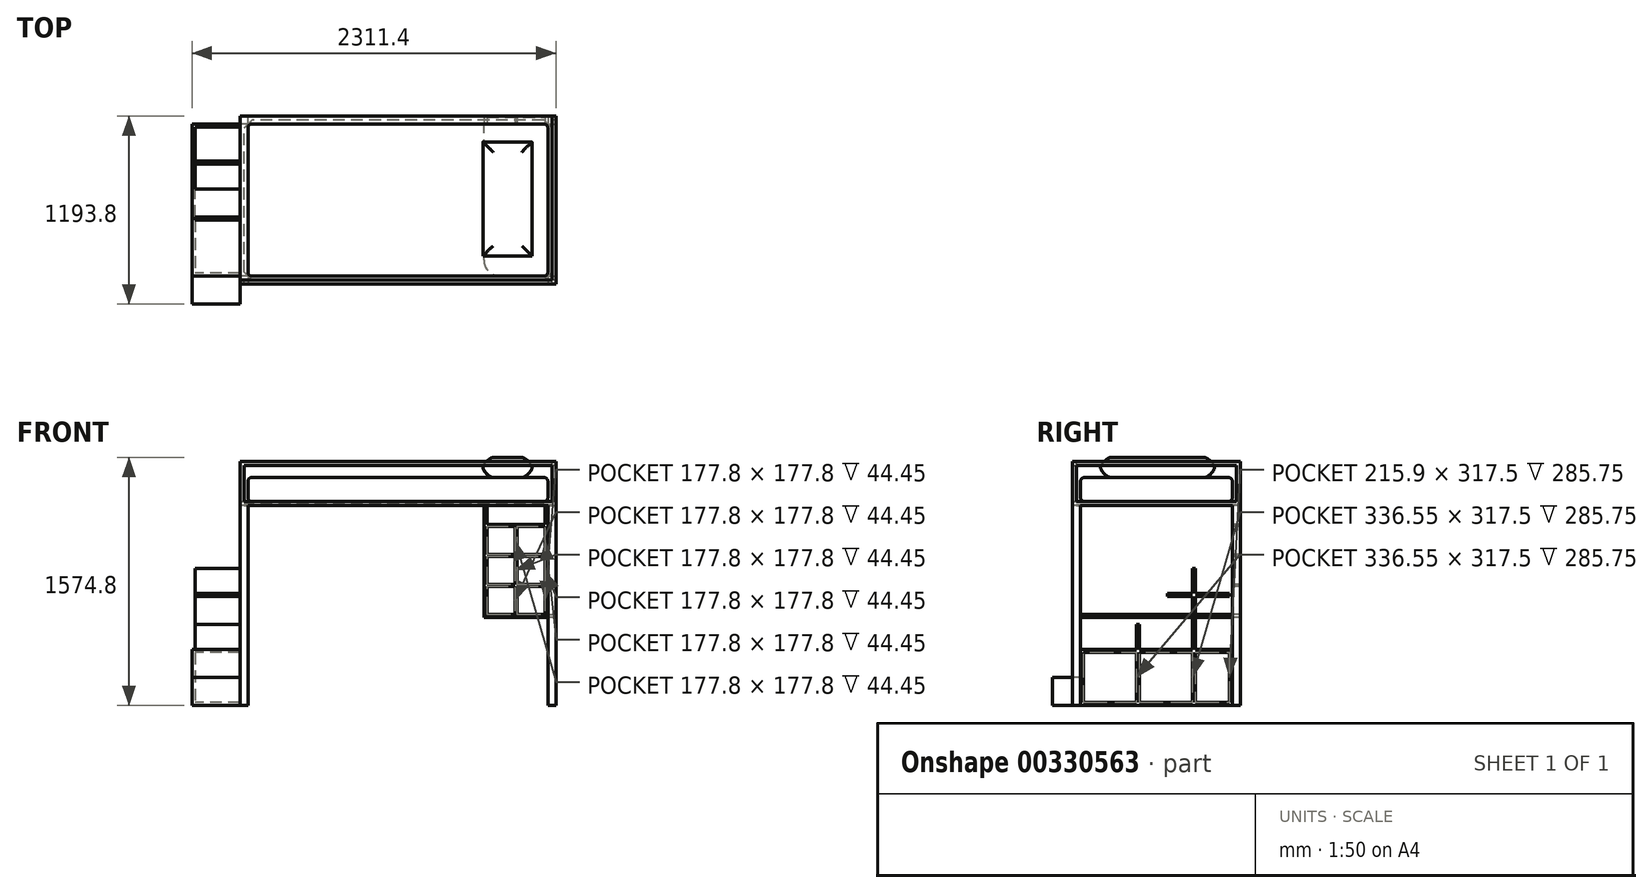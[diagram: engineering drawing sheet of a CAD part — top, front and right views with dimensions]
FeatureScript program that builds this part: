
annotation { "Feature Type Name" : "Feature", "Feature Type Description" : "" }
export const myFeature = defineFeature(function(context is Context, id is Id, definition is map)
    precondition{}
    {
        {
            var Q0;
            Q0=qCreatedBy(makeId("Top.planeOp"),FACE);
            var sketch = newSketch(context, id + "F0", { "sketchPlane" : qUnion([Q0])});
            skLineSegment(sketch, "E0.bottom", {"start": v(-952.5, 482.6) * mm, "end": v(952.5, 482.6) * mm});
            skLineSegment(sketch, "E0.top", {"start": v(-952.5, -482.6) * mm, "end": v(952.5, -482.6) * mm});
            skLineSegment(sketch, "E0.left", {"start": v(-952.5, 482.6) * mm, "end": v(-952.5, -482.6) * mm});
            skLineSegment(sketch, "E0.right", {"start": v(952.5, 482.6) * mm, "end": v(952.5, -482.6) * mm});
            skPoint(sketch, "E0.middle", {"position": v(0, 0) * mm});
            skLineSegment(sketch, "E1.bottom", {"start": v(-952.5, 482.6) * mm, "end": v(-1003.3, 482.6) * mm});
            skLineSegment(sketch, "E1.top", {"start": v(-952.5, 533.4) * mm, "end": v(-1003.3, 533.4) * mm});
            skLineSegment(sketch, "E1.left", {"start": v(-952.5, 482.6) * mm, "end": v(-952.5, 533.4) * mm});
            skLineSegment(sketch, "E1.right", {"start": v(-1003.3, 482.6) * mm, "end": v(-1003.3, 533.4) * mm});
            skLineSegment(sketch, "E2.bottom", {"start": v(-952.5, -482.6) * mm, "end": v(-1003.3, -482.6) * mm});
            skLineSegment(sketch, "E2.top", {"start": v(-952.5, -533.4) * mm, "end": v(-1003.3, -533.4) * mm});
            skLineSegment(sketch, "E2.left", {"start": v(-952.5, -482.6) * mm, "end": v(-952.5, -533.4) * mm});
            skLineSegment(sketch, "E2.right", {"start": v(-1003.3, -482.6) * mm, "end": v(-1003.3, -533.4) * mm});
            skLineSegment(sketch, "E3.bottom", {"start": v(952.5, 482.6) * mm, "end": v(1003.3, 482.6) * mm});
            skLineSegment(sketch, "E3.top", {"start": v(952.5, 533.4) * mm, "end": v(1003.3, 533.4) * mm});
            skLineSegment(sketch, "E3.left", {"start": v(952.5, 482.6) * mm, "end": v(952.5, 533.4) * mm});
            skLineSegment(sketch, "E3.right", {"start": v(1003.3, 482.6) * mm, "end": v(1003.3, 533.4) * mm});
            skLineSegment(sketch, "E4.bottom", {"start": v(952.5, -482.6) * mm, "end": v(1003.3, -482.6) * mm});
            skLineSegment(sketch, "E4.top", {"start": v(952.5, -533.4) * mm, "end": v(1003.3, -533.4) * mm});
            skLineSegment(sketch, "E4.left", {"start": v(952.5, -482.6) * mm, "end": v(952.5, -533.4) * mm});
            skLineSegment(sketch, "E4.right", {"start": v(1003.3, -482.6) * mm, "end": v(1003.3, -533.4) * mm});
            skSolve(sketch);
        }
        {
            var Q0;
            Q0=makeQuery(id+"F0.imprint","IMPRINT",FACE,{"disambiguationData":[TD([[makeQuery(id+"F0.imprint","IMPRINT",EDGE,{"derivedFrom":sQuery(id+"F0.wireOp",EDGE,"E1.bottom")}),-1.0]])]});
            var Q1;
            Q1=makeQuery(id+"F0.imprint","IMPRINT",FACE,{"disambiguationData":[TD([[makeQuery(id+"F0.imprint","IMPRINT",EDGE,{"derivedFrom":sQuery(id+"F0.wireOp",EDGE,"E2.bottom")}),1.0]])]});
            var Q2;
            Q2=makeQuery(id+"F0.imprint","IMPRINT",FACE,{"disambiguationData":[TD([[makeQuery(id+"F0.imprint","IMPRINT",EDGE,{"derivedFrom":sQuery(id+"F0.wireOp",EDGE,"E3.bottom")}),1.0]])]});
            var Q3;
            Q3=makeQuery(id+"F0.imprint","IMPRINT",FACE,{"disambiguationData":[TD([[makeQuery(id+"F0.imprint","IMPRINT",EDGE,{"derivedFrom":sQuery(id+"F0.wireOp",EDGE,"E4.bottom")}),-1.0]])]});
            extrude(context, id + "F1", {"entities" : qUnion([Q0, Q1, Q2, Q3]), "depth" : 1270 * mm});
        }
        {
            var Q0;
            Q0=makeQuery(id+"F1.opExtrude","SWEPT_FACE",FACE,{"disambiguationData":[OSD([sQuery(id+"F0.wireOp",EDGE,"E1.right")])]});
            cPlane(context, id + "F2", {"entities" : qUnion([Q0]), "cplaneType" : CPlaneType.OFFSET, "offset" : 304.8 * mm, "width" : 152.4 * mm, "height" : 152.4 * mm});
        }
        {
            var Q0;
            Q0=qCreatedBy(id+"F2.planeOp",FACE);
            var sketch = newSketch(context, id + "F3", { "sketchPlane" : qUnion([Q0])});
            skPoint(sketch, "E5.0", {"position": v(-482.6, 0) * mm});
            skPoint(sketch, "E6.0", {"position": v(482.6, 0) * mm});
            skLineSegment(sketch, "E7.bottom", {"start": v(-482.6, 0) * mm, "end": v(482.6, 0) * mm});
            skLineSegment(sketch, "E7.top", {"start": v(-482.6, 355.6) * mm, "end": v(482.6, 355.6) * mm});
            skLineSegment(sketch, "E7.left", {"start": v(-482.6, 0) * mm, "end": v(-482.6, 355.6) * mm});
            skLineSegment(sketch, "E7.right", {"start": v(482.6, 0) * mm, "end": v(482.6, 147.48) * mm});
            skLineSegment(sketch, "E8.bottom", {"start": v(-482.6, 355.6) * mm, "end": v(127, 355.6) * mm});
            skLineSegment(sketch, "E8.top", {"start": v(-482.6, 711.2) * mm, "end": v(127, 711.2) * mm});
            skLineSegment(sketch, "E8.left", {"start": v(-482.6, 355.6) * mm, "end": v(-482.6, 711.2) * mm});
            skLineSegment(sketch, "E8.right", {"start": v(127, 355.6) * mm, "end": v(127, 711.2) * mm});
            skLineSegment(sketch, "E9.bottom", {"start": v(-482.6, 711.2) * mm, "end": v(-228.6, 711.2) * mm});
            skLineSegment(sketch, "E9.top", {"start": v(-482.6, 1066.8) * mm, "end": v(-228.6, 1066.8) * mm});
            skLineSegment(sketch, "E9.left", {"start": v(-482.6, 711.2) * mm, "end": v(-482.6, 1066.8) * mm});
            skLineSegment(sketch, "E9.right", {"start": v(-228.6, 711.2) * mm, "end": v(-228.6, 1066.8) * mm});
            skLineSegment(sketch, "E10.bottom", {"start": v(127, 355.6) * mm, "end": v(304.8, 355.6) * mm});
            skLineSegment(sketch, "E10.top", {"start": v(127, 533.4) * mm, "end": v(304.8, 533.4) * mm});
            skLineSegment(sketch, "E10.left", {"start": v(127, 355.6) * mm, "end": v(127, 533.4) * mm});
            skLineSegment(sketch, "E10.right", {"start": v(304.8, 355.6) * mm, "end": v(304.8, 533.4) * mm});
            skLineSegment(sketch, "E11.bottom", {"start": v(482.6, 0) * mm, "end": v(660.4, 0) * mm});
            skLineSegment(sketch, "E11.top", {"start": v(482.6, 177.8) * mm, "end": v(660.4, 177.8) * mm});
            skLineSegment(sketch, "E11.left", {"start": v(482.6, 0) * mm, "end": v(482.6, 177.8) * mm});
            skLineSegment(sketch, "E11.right", {"start": v(660.4, 0) * mm, "end": v(660.4, 177.8) * mm});
            skLineSegment(sketch, "E12.bottom", {"start": v(-228.6, 711.2) * mm, "end": v(-50.8, 711.2) * mm});
            skLineSegment(sketch, "E12.top", {"start": v(-228.6, 889) * mm, "end": v(-50.8, 889) * mm});
            skLineSegment(sketch, "E12.left", {"start": v(-228.6, 711.2) * mm, "end": v(-228.6, 889) * mm});
            skLineSegment(sketch, "E12.right", {"start": v(-50.8, 711.2) * mm, "end": v(-50.8, 889) * mm});
            skLineSegment(sketch, "E13", {"start": v(482.6, 355.6) * mm, "end": v(482.6, 177.8) * mm});
            skSolve(sketch);
        }
        {
            var Q0;
            Q0=makeQuery(id+"F3.imprint","IMPRINT",FACE,{"disambiguationData":[TD([[makeQuery(id+"F3.imprint","IMPRINT",EDGE,{"derivedFrom":sQuery(id+"F3.wireOp",EDGE,"E9.bottom")}),1.0]])]});
            var Q1;
            Q1=makeQuery(id+"F3.imprint","IMPRINT",FACE,{"disambiguationData":[TD([[makeQuery(id+"F3.imprint","IMPRINT",EDGE,{"derivedFrom":sQuery(id+"F3.wireOp",EDGE,"E12.bottom")}),1.0]])]});
            var Q2;
            Q2=makeQuery(id+"F3.imprint","IMPRINT",FACE,{"disambiguationData":[TD([[makeQuery(id+"F3.imprint","IMPRINT",EDGE,{"derivedFrom":sQuery(id+"F3.wireOp",EDGE,"E8.bottom")}),1.0]])]});
            var Q3;
            Q3=makeQuery(id+"F3.imprint","IMPRINT",FACE,{"disambiguationData":[TD([[makeQuery(id+"F3.imprint","IMPRINT",EDGE,{"derivedFrom":sQuery(id+"F3.wireOp",EDGE,"E10.bottom")}),1.0]])]});
            var Q4;
            {var subQ1=sQuery(id+"F3.wireOp",EDGE,"E7.bottom");Q4=makeQuery(id+"F3.imprint","IMPRINT",FACE,{"disambiguationData":[TD([[makeQuery(id+"F3.imprint","IMPRINT",EDGE,{"derivedFrom":subQ1}),1.0]])]});}
            var Q5;
            {var subQ3=sQuery(id+"F3.wireOp",EDGE,"E11.bottom");Q5=makeQuery(id+"F3.imprint","IMPRINT",FACE,{"disambiguationData":[TD([[makeQuery(id+"F3.imprint","IMPRINT",EDGE,{"derivedFrom":subQ3}),1.0]])]});}
            extrude(context, id + "F4", {"entities" : qUnion([Q0, Q1, Q2, Q3, Q4, Q5]), "oppositeDirection" : true, "depth" : 19.05 * mm});
        }
        {
            var Q0;
            Q0=makeQuery(id+"F4.opExtrude","CAP_FACE",FACE,{"disambiguationData":[OSD([sQuery(id+"F3.wireOp",EDGE,"E7.bottom"),sQuery(id+"F3.wireOp",EDGE,"E7.top"),sQuery(id+"F3.wireOp",EDGE,"E7.left"),sQuery(id+"F3.wireOp",EDGE,"E8.top"),sQuery(id+"F3.wireOp",EDGE,"E8.left"),sQuery(id+"F3.wireOp",EDGE,"E8.right"),sQuery(id+"F3.wireOp",EDGE,"E9.top"),sQuery(id+"F3.wireOp",EDGE,"E9.left"),sQuery(id+"F3.wireOp",EDGE,"E9.right"),sQuery(id+"F3.wireOp",EDGE,"E10.top"),sQuery(id+"F3.wireOp",EDGE,"E10.right"),sQuery(id+"F3.wireOp",EDGE,"E11.bottom"),sQuery(id+"F3.wireOp",EDGE,"E11.top"),sQuery(id+"F3.wireOp",EDGE,"E11.right"),sQuery(id+"F3.wireOp",EDGE,"E12.top"),sQuery(id+"F3.wireOp",EDGE,"E12.right"),sQuery(id+"F3.wireOp",EDGE,"E13")])],"isStart":false});
            var sketch = newSketch(context, id + "F5", { "sketchPlane" : qUnion([Q0])});
            skLineSegment(sketch, "E14.0", {"start": v(-463.55, 19.05) * mm, "end": v(463.55, 19.05) * mm});
            skLineSegment(sketch, "E14.1", {"start": v(69.85, 869.95) * mm, "end": v(69.85, 692.15) * mm});
            skLineSegment(sketch, "E14.2", {"start": v(247.65, 869.95) * mm, "end": v(69.85, 869.95) * mm});
            skLineSegment(sketch, "E14.3", {"start": v(247.65, 1047.75) * mm, "end": v(247.65, 869.95) * mm});
            skLineSegment(sketch, "E14.4", {"start": v(463.55, 1047.75) * mm, "end": v(247.65, 1047.75) * mm});
            skLineSegment(sketch, "E14.5", {"start": v(69.85, 692.15) * mm, "end": v(-107.95, 692.15) * mm});
            skLineSegment(sketch, "E14.6", {"start": v(463.55, 19.05) * mm, "end": v(463.55, 1047.75) * mm});
            skLineSegment(sketch, "E14.7", {"start": v(-107.95, 692.15) * mm, "end": v(-107.95, 514.35) * mm});
            skLineSegment(sketch, "E14.8", {"start": v(-107.95, 514.35) * mm, "end": v(-285.75, 514.35) * mm});
            skLineSegment(sketch, "E14.9", {"start": v(-285.75, 514.35) * mm, "end": v(-285.75, 336.55) * mm});
            skLineSegment(sketch, "E14.10", {"start": v(-285.75, 336.55) * mm, "end": v(-463.55, 336.55) * mm});
            skLineSegment(sketch, "E14.11", {"start": v(-463.55, 336.55) * mm, "end": v(-463.55, 19.05) * mm});
            skLineSegment(sketch, "E15.0.0", {"start": v(482.6, 0) * mm, "end": v(482.6, 1066.8) * mm});
            skLineSegment(sketch, "E15.0.1", {"start": v(482.6, 1066.8) * mm, "end": v(228.6, 1066.8) * mm});
            skLineSegment(sketch, "E15.0.2", {"start": v(228.6, 1066.8) * mm, "end": v(228.6, 889) * mm});
            skLineSegment(sketch, "E15.0.3", {"start": v(228.6, 889) * mm, "end": v(50.8, 889) * mm});
            skLineSegment(sketch, "E15.0.4", {"start": v(50.8, 889) * mm, "end": v(50.8, 711.2) * mm});
            skLineSegment(sketch, "E15.0.5", {"start": v(50.8, 711.2) * mm, "end": v(-127, 711.2) * mm});
            skLineSegment(sketch, "E15.0.6", {"start": v(-127, 711.2) * mm, "end": v(-127, 533.4) * mm});
            skLineSegment(sketch, "E15.0.7", {"start": v(-127, 533.4) * mm, "end": v(-304.8, 533.4) * mm});
            skLineSegment(sketch, "E15.0.8", {"start": v(-304.8, 533.4) * mm, "end": v(-304.8, 355.6) * mm});
            skLineSegment(sketch, "E15.0.9", {"start": v(-304.8, 355.6) * mm, "end": v(-482.6, 355.6) * mm});
            skLineSegment(sketch, "E15.0.10", {"start": v(-482.6, 355.6) * mm, "end": v(-482.6, 177.8) * mm});
            skLineSegment(sketch, "E15.0.11", {"start": v(-482.6, 177.8) * mm, "end": v(-660.4, 177.8) * mm});
            skLineSegment(sketch, "E15.0.12", {"start": v(-660.4, 177.8) * mm, "end": v(-660.4, 0) * mm});
            skLineSegment(sketch, "E15.0.13", {"start": v(-660.4, 0) * mm, "end": v(482.6, 0) * mm});
            skSolve(sketch);
        }
        {
            var Q0;
            Q0=makeQuery(id+"F5.imprint","IMPRINT",FACE,{"disambiguationData":[TD([[makeQuery(id+"F5.imprint","IMPRINT",EDGE,{"derivedFrom":sQuery(id+"F5.wireOp",EDGE,"E14.0")}),-1.0]])]});
            extrude(context, id + "F6", {"entities" : qUnion([Q0]), "operationType" : NewBodyOperationType.ADD, "depth" : 285.75 * mm});
        }
        {
            var Q0;
            Q0=makeQuery(id+"F4.opExtrude","CAP_FACE",FACE,{"disambiguationData":[OSD([sQuery(id+"F3.wireOp",EDGE,"E7.bottom"),sQuery(id+"F3.wireOp",EDGE,"E7.top"),sQuery(id+"F3.wireOp",EDGE,"E7.left"),sQuery(id+"F3.wireOp",EDGE,"E8.top"),sQuery(id+"F3.wireOp",EDGE,"E8.left"),sQuery(id+"F3.wireOp",EDGE,"E8.right"),sQuery(id+"F3.wireOp",EDGE,"E9.top"),sQuery(id+"F3.wireOp",EDGE,"E9.left"),sQuery(id+"F3.wireOp",EDGE,"E9.right"),sQuery(id+"F3.wireOp",EDGE,"E10.top"),sQuery(id+"F3.wireOp",EDGE,"E10.right"),sQuery(id+"F3.wireOp",EDGE,"E11.bottom"),sQuery(id+"F3.wireOp",EDGE,"E11.top"),sQuery(id+"F3.wireOp",EDGE,"E11.right"),sQuery(id+"F3.wireOp",EDGE,"E12.top"),sQuery(id+"F3.wireOp",EDGE,"E12.right"),sQuery(id+"F3.wireOp",EDGE,"E13")])],"isStart":false});
            var sketch = newSketch(context, id + "F7", { "sketchPlane" : qUnion([Q0])});
            skLineSegment(sketch, "E16.bottom", {"start": v(-285.75, 336.55) * mm, "end": v(463.55, 336.55) * mm});
            skLineSegment(sketch, "E16.top", {"start": v(-285.75, 355.6) * mm, "end": v(463.55, 355.6) * mm});
            skLineSegment(sketch, "E16.left", {"start": v(-285.75, 336.55) * mm, "end": v(-285.75, 355.6) * mm});
            skLineSegment(sketch, "E16.right", {"start": v(463.55, 336.55) * mm, "end": v(463.55, 355.6) * mm});
            skLineSegment(sketch, "E17.bottom", {"start": v(-107.95, 514.35) * mm, "end": v(-127, 514.35) * mm});
            skLineSegment(sketch, "E17.top", {"start": v(-107.95, 19.05) * mm, "end": v(-127, 19.05) * mm});
            skLineSegment(sketch, "E17.left", {"start": v(-107.95, 514.35) * mm, "end": v(-107.95, 19.05) * mm});
            skLineSegment(sketch, "E17.right", {"start": v(-127, 514.35) * mm, "end": v(-127, 19.05) * mm});
            skLineSegment(sketch, "E18.bottom", {"start": v(247.65, 869.95) * mm, "end": v(228.6, 869.95) * mm});
            skLineSegment(sketch, "E18.top", {"start": v(247.65, 19.05) * mm, "end": v(228.6, 19.05) * mm});
            skLineSegment(sketch, "E18.left", {"start": v(247.65, 869.95) * mm, "end": v(247.65, 19.05) * mm});
            skLineSegment(sketch, "E18.right", {"start": v(228.6, 869.95) * mm, "end": v(228.6, 19.05) * mm});
            skLineSegment(sketch, "E19.bottom", {"start": v(69.85, 692.15) * mm, "end": v(463.55, 692.15) * mm});
            skLineSegment(sketch, "E19.top", {"start": v(69.85, 711.2) * mm, "end": v(463.55, 711.2) * mm});
            skLineSegment(sketch, "E19.left", {"start": v(69.85, 692.15) * mm, "end": v(69.85, 711.2) * mm});
            skLineSegment(sketch, "E19.right", {"start": v(463.55, 692.15) * mm, "end": v(463.55, 711.2) * mm});
            skSolve(sketch);
        }
        {
            var Q0;
            Q0 = qSketchRegion(id + "F7", true);
            extrude(context, id + "F8", {"entities" : qUnion([Q0]), "operationType" : NewBodyOperationType.ADD, "depth" : 285.75 * mm});
        }
        {
            var Q0;
            Q0=makeQuery(id+"F1.opExtrude","CAP_FACE",FACE,{"disambiguationData":[OSD([sQuery(id+"F0.wireOp",EDGE,"E1.bottom"),sQuery(id+"F0.wireOp",EDGE,"E1.top"),sQuery(id+"F0.wireOp",EDGE,"E1.left"),sQuery(id+"F0.wireOp",EDGE,"E1.right")])],"isStart":false});
            var sketch = newSketch(context, id + "F9", { "sketchPlane" : qUnion([Q0])});
            skPoint(sketch, "E20.0", {"position": v(1003.3, -533.4) * mm});
            skPoint(sketch, "E21.0", {"position": v(-1003.3, 533.4) * mm});
            skLineSegment(sketch, "E22.bottom", {"start": v(-1003.3, 533.4) * mm, "end": v(1003.3, 533.4) * mm});
            skLineSegment(sketch, "E22.top", {"start": v(-1003.3, -533.4) * mm, "end": v(1003.3, -533.4) * mm});
            skLineSegment(sketch, "E22.left", {"start": v(-1003.3, 533.4) * mm, "end": v(-1003.3, -533.4) * mm});
            skLineSegment(sketch, "E22.right", {"start": v(1003.3, 533.4) * mm, "end": v(1003.3, -533.4) * mm});
            skLineSegment(sketch, "E23.0.0", {"start": v(1003.3, -482.6) * mm, "end": v(952.5, -482.6) * mm});
            skLineSegment(sketch, "E23.0.1", {"start": v(952.5, -482.6) * mm, "end": v(952.5, -533.4) * mm});
            skLineSegment(sketch, "E23.0.2", {"start": v(952.5, -533.4) * mm, "end": v(1003.3, -533.4) * mm});
            skLineSegment(sketch, "E23.0.3", {"start": v(1003.3, -533.4) * mm, "end": v(1003.3, -482.6) * mm});
            skLineSegment(sketch, "E24.0.0", {"start": v(1003.3, 533.4) * mm, "end": v(952.5, 533.4) * mm});
            skLineSegment(sketch, "E24.0.1", {"start": v(952.5, 533.4) * mm, "end": v(952.5, 482.6) * mm});
            skLineSegment(sketch, "E24.0.2", {"start": v(952.5, 482.6) * mm, "end": v(1003.3, 482.6) * mm});
            skLineSegment(sketch, "E24.0.3", {"start": v(1003.3, 482.6) * mm, "end": v(1003.3, 533.4) * mm});
            skLineSegment(sketch, "E25.0.0", {"start": v(-952.5, -533.4) * mm, "end": v(-952.5, -482.6) * mm});
            skLineSegment(sketch, "E25.0.1", {"start": v(-952.5, -482.6) * mm, "end": v(-1003.3, -482.6) * mm});
            skLineSegment(sketch, "E25.0.2", {"start": v(-1003.3, -482.6) * mm, "end": v(-1003.3, -533.4) * mm});
            skLineSegment(sketch, "E25.0.3", {"start": v(-1003.3, -533.4) * mm, "end": v(-952.5, -533.4) * mm});
            skLineSegment(sketch, "E26.0.0", {"start": v(-952.5, 482.6) * mm, "end": v(-952.5, 533.4) * mm});
            skLineSegment(sketch, "E26.0.1", {"start": v(-952.5, 533.4) * mm, "end": v(-1003.3, 533.4) * mm});
            skLineSegment(sketch, "E26.0.2", {"start": v(-1003.3, 533.4) * mm, "end": v(-1003.3, 482.6) * mm});
            skLineSegment(sketch, "E26.0.3", {"start": v(-1003.3, 482.6) * mm, "end": v(-952.5, 482.6) * mm});
            skPoint(sketch, "E27.firstSnap0", {"position": v(952.5, -508) * mm});
            skPoint(sketch, "E27.firstSnap1", {"position": v(977.9, -482.6) * mm});
            skPoint(sketch, "E27.oppositeSnap0", {"position": v(-1003.3, 508) * mm});
            skPoint(sketch, "E27.oppositeSnap1", {"position": v(-977.9, 533.4) * mm});
            skLineSegment(sketch, "E27.bottom", {"start": v(977.9, -508) * mm, "end": v(-977.9, -508) * mm});
            skLineSegment(sketch, "E27.top", {"start": v(977.9, 508) * mm, "end": v(-977.9, 508) * mm});
            skLineSegment(sketch, "E27.left", {"start": v(977.9, -508) * mm, "end": v(977.9, 508) * mm});
            skLineSegment(sketch, "E27.right", {"start": v(-977.9, -508) * mm, "end": v(-977.9, 508) * mm});
            skSolve(sketch);
        }
        {
            var Q0;
            Q0 = qSketchRegion(id + "F9", true);
            extrude(context, id + "F10", {"entities" : qUnion([Q0]), "depth" : 25.4 * mm});
        }
        {
            var Q0;
            Q0=makeQuery(id+"F10.opExtrude","CAP_FACE",FACE,{"disambiguationData":[OSD([sQuery(id+"F9.wireOp",EDGE,"E22.bottom"),sQuery(id+"F9.wireOp",EDGE,"E22.top"),sQuery(id+"F9.wireOp",EDGE,"E22.left"),sQuery(id+"F9.wireOp",EDGE,"E22.right")])],"isStart":false});
            var sketch = newSketch(context, id + "F11", { "sketchPlane" : qUnion([Q0])});
            skPoint(sketch, "E28.0", {"position": v(-952.5, 482.6) * mm});
            skPoint(sketch, "E29.0", {"position": v(952.5, -482.6) * mm});
            skLineSegment(sketch, "E30.bottom", {"start": v(-952.5, 482.6) * mm, "end": v(952.5, 482.6) * mm});
            skLineSegment(sketch, "E30.top", {"start": v(-952.5, -482.6) * mm, "end": v(952.5, -482.6) * mm});
            skLineSegment(sketch, "E30.left", {"start": v(-952.5, 482.6) * mm, "end": v(-952.5, -482.6) * mm});
            skLineSegment(sketch, "E30.right", {"start": v(952.5, 482.6) * mm, "end": v(952.5, -482.6) * mm});
            skSolve(sketch);
        }
        {
            var Q0;
            Q0=makeQuery(id+"F11.imprint","IMPRINT",FACE,{"disambiguationData":[TD([[makeQuery(id+"F11.imprint","IMPRINT",EDGE,{"derivedFrom":sQuery(id+"F11.wireOp",EDGE,"E30.bottom")}),-1.0]])]});
            extrude(context, id + "F12", {"entities" : qUnion([Q0]), "depth" : 152.4 * mm});
        }
        {
            var Q0;
            Q0=makeQuery(id+"F12.opExtrude","SWEPT_EDGE",EDGE,{"disambiguationData":[OSD([sQuery(id+"F11.wireOp",EDGE,"E30.top"),sQuery(id+"F11.wireOp",EDGE,"E30.left")])]});
            var Q1;
            Q1=makeQuery(id+"F12.opExtrude","SWEPT_EDGE",EDGE,{"disambiguationData":[OSD([sQuery(id+"F11.wireOp",EDGE,"E30.top"),sQuery(id+"F11.wireOp",EDGE,"E30.right")])]});
            var Q2;
            Q2=makeQuery(id+"F12.opExtrude","SWEPT_EDGE",EDGE,{"disambiguationData":[OSD([sQuery(id+"F11.wireOp",EDGE,"E30.bottom"),sQuery(id+"F11.wireOp",EDGE,"E30.right")])]});
            var Q3;
            Q3=makeQuery(id+"F12.opExtrude","SWEPT_EDGE",EDGE,{"disambiguationData":[OSD([sQuery(id+"F11.wireOp",EDGE,"E30.bottom"),sQuery(id+"F11.wireOp",EDGE,"E30.left")])]});
            var Q4;
            Q4=makeQuery(id+"F12.opExtrude","CAP_EDGE",EDGE,{"disambiguationData":[OSD([sQuery(id+"F11.wireOp",EDGE,"E30.left")])],"isStart":false});
            var Q5;
            Q5=makeQuery(id+"F12.opExtrude","CAP_EDGE",EDGE,{"disambiguationData":[OSD([sQuery(id+"F11.wireOp",EDGE,"E30.bottom")])],"isStart":false});
            var Q6;
            Q6=makeQuery(id+"F12.opExtrude","CAP_EDGE",EDGE,{"disambiguationData":[OSD([sQuery(id+"F11.wireOp",EDGE,"E30.right")])],"isStart":false});
            var Q7;
            Q7=makeQuery(id+"F12.opExtrude","CAP_EDGE",EDGE,{"disambiguationData":[OSD([sQuery(id+"F11.wireOp",EDGE,"E30.top")])],"isStart":false});
            var Q8;
            Q8=makeQuery(id+"F12.opExtrude","CAP_EDGE",EDGE,{"disambiguationData":[OSD([sQuery(id+"F11.wireOp",EDGE,"E30.top")])],"isStart":true});
            var Q9;
            Q9=makeQuery(id+"F12.opExtrude","CAP_EDGE",EDGE,{"disambiguationData":[OSD([sQuery(id+"F11.wireOp",EDGE,"E30.right")])],"isStart":true});
            var Q10;
            Q10=makeQuery(id+"F12.opExtrude","CAP_EDGE",EDGE,{"disambiguationData":[OSD([sQuery(id+"F11.wireOp",EDGE,"E30.bottom")])],"isStart":true});
            var Q11;
            Q11=makeQuery(id+"F12.opExtrude","CAP_EDGE",EDGE,{"disambiguationData":[OSD([sQuery(id+"F11.wireOp",EDGE,"E30.left")])],"isStart":true});
            fillet(context, id + "F13", {"entities" : qUnion([Q0, Q1, Q2, Q3, Q4, Q5, Q6, Q7, Q8, Q9, Q10, Q11]), "radius" : 25.4 * mm, "tangentPropagation" : true, "allowEdgeOverflow" : false});
        }
        {
            var Q0;
            Q0=makeQuery(id+"F10.opExtrude","CAP_FACE",FACE,{"disambiguationData":[OSD([sQuery(id+"F9.wireOp",EDGE,"E22.bottom"),sQuery(id+"F9.wireOp",EDGE,"E22.top"),sQuery(id+"F9.wireOp",EDGE,"E22.left"),sQuery(id+"F9.wireOp",EDGE,"E22.right"),sQuery(id+"F9.wireOp",EDGE,"E23.0.2"),sQuery(id+"F9.wireOp",EDGE,"E23.0.3"),sQuery(id+"F9.wireOp",EDGE,"E24.0.0"),sQuery(id+"F9.wireOp",EDGE,"E24.0.3"),sQuery(id+"F9.wireOp",EDGE,"E25.0.2"),sQuery(id+"F9.wireOp",EDGE,"E25.0.3"),sQuery(id+"F9.wireOp",EDGE,"E26.0.1"),sQuery(id+"F9.wireOp",EDGE,"E26.0.2"),sQuery(id+"F9.wireOp",EDGE,"E27.bottom"),sQuery(id+"F9.wireOp",EDGE,"E27.top"),sQuery(id+"F9.wireOp",EDGE,"E27.left"),sQuery(id+"F9.wireOp",EDGE,"E27.right")])],"isStart":true});
            var sketch = newSketch(context, id + "F14", { "sketchPlane" : qUnion([Q0])});
            skLineSegment(sketch, "E31.0", {"start": v(977.9, 508) * mm, "end": v(-977.9, 508) * mm});
            skLineSegment(sketch, "E32.0", {"start": v(-977.9, 508) * mm, "end": v(-977.9, -508) * mm});
            skLineSegment(sketch, "E33", {"start": v(-977.9, 508) * mm, "end": v(-927.1, 508) * mm});
            skLineSegment(sketch, "E34", {"start": v(-927.1, 508) * mm, "end": v(-977.9, 457.2) * mm});
            skLineSegment(sketch, "E35", {"start": v(-977.9, 457.2) * mm, "end": v(-977.9, 508) * mm});
            skLineSegment(sketch, "E36", {"start": v(-977.9, -508) * mm, "end": v(-977.9, -457.2) * mm});
            skLineSegment(sketch, "E37", {"start": v(-977.9, -457.2) * mm, "end": v(-927.1, -508) * mm});
            skLineSegment(sketch, "E38", {"start": v(-927.1, -508) * mm, "end": v(-977.9, -508) * mm});
            skLineSegment(sketch, "E39", {"start": v(977.9, -508) * mm, "end": v(927.1, -508) * mm});
            skLineSegment(sketch, "E40", {"start": v(927.1, -508) * mm, "end": v(977.9, -457.2) * mm});
            skLineSegment(sketch, "E41", {"start": v(977.9, -457.2) * mm, "end": v(977.9, -508) * mm});
            skLineSegment(sketch, "E42", {"start": v(977.9, 508) * mm, "end": v(927.1, 508) * mm});
            skLineSegment(sketch, "E43", {"start": v(927.1, 508) * mm, "end": v(977.9, 457.2) * mm});
            skLineSegment(sketch, "E44", {"start": v(977.9, 457.2) * mm, "end": v(977.9, 508) * mm});
            skLineSegment(sketch, "E45", {"start": v(927.1, 508) * mm, "end": v(977.9, 508) * mm});
            skLineSegment(sketch, "E46", {"start": v(977.9, 508) * mm, "end": v(977.9, 457.2) * mm});
            skSolve(sketch);
        }
        {
            var Q0;
            Q0 = qSketchRegion(id + "F14", true);
            extrude(context, id + "F15", {"entities" : qUnion([Q0]), "operationType" : NewBodyOperationType.ADD, "oppositeDirection" : true, "depth" : 6.35 * mm});
        }
        {
            var Q0;
            Q0=makeQuery(id+"F15.opExtrude","CAP_FACE",FACE,{"disambiguationData":[OSD([sQuery(id+"F14.wireOp",EDGE,"E33"),sQuery(id+"F14.wireOp",EDGE,"E34"),sQuery(id+"F14.wireOp",EDGE,"E35")])],"isStart":false});
            var sketch = newSketch(context, id + "F16", { "sketchPlane" : qUnion([Q0])});
            skLineSegment(sketch, "E47.0.0", {"start": v(-977.9, 457.2) * mm, "end": v(-927.1, 508) * mm});
            skLineSegment(sketch, "E47.0.1", {"start": v(-927.1, 508) * mm, "end": v(-977.9, 508) * mm});
            skLineSegment(sketch, "E47.0.2", {"start": v(-977.9, 508) * mm, "end": v(-977.9, 457.2) * mm});
            skLineSegment(sketch, "E48.0.0", {"start": v(927.1, -508) * mm, "end": v(977.9, -508) * mm});
            skLineSegment(sketch, "E48.0.1", {"start": v(977.9, -508) * mm, "end": v(977.9, -457.2) * mm});
            skLineSegment(sketch, "E48.0.2", {"start": v(977.9, -457.2) * mm, "end": v(927.1, -508) * mm});
            skLineSegment(sketch, "E49.bottom", {"start": v(-977.9, 508) * mm, "end": v(977.9, 508) * mm});
            skLineSegment(sketch, "E49.top", {"start": v(-977.9, -508) * mm, "end": v(977.9, -508) * mm});
            skLineSegment(sketch, "E49.left", {"start": v(-977.9, 508) * mm, "end": v(-977.9, -508) * mm});
            skLineSegment(sketch, "E49.right", {"start": v(977.9, 508) * mm, "end": v(977.9, -508) * mm});
            skSolve(sketch);
        }
        {
            var Q0;
            Q0 = qSketchRegion(id + "F16", true);
            extrude(context, id + "F17", {"entities" : qUnion([Q0]), "depth" : 19.05 * mm});
        }
        {
            var Q0;
            Q0=makeQuery(id+"F10.opExtrude","CAP_FACE",FACE,{"disambiguationData":[OSD([sQuery(id+"F9.wireOp",EDGE,"E22.bottom"),sQuery(id+"F9.wireOp",EDGE,"E22.top"),sQuery(id+"F9.wireOp",EDGE,"E22.left"),sQuery(id+"F9.wireOp",EDGE,"E22.right"),sQuery(id+"F9.wireOp",EDGE,"E23.0.2"),sQuery(id+"F9.wireOp",EDGE,"E23.0.3"),sQuery(id+"F9.wireOp",EDGE,"E24.0.0"),sQuery(id+"F9.wireOp",EDGE,"E24.0.3"),sQuery(id+"F9.wireOp",EDGE,"E25.0.2"),sQuery(id+"F9.wireOp",EDGE,"E25.0.3"),sQuery(id+"F9.wireOp",EDGE,"E26.0.1"),sQuery(id+"F9.wireOp",EDGE,"E26.0.2"),sQuery(id+"F9.wireOp",EDGE,"E27.bottom"),sQuery(id+"F9.wireOp",EDGE,"E27.top"),sQuery(id+"F9.wireOp",EDGE,"E27.left"),sQuery(id+"F9.wireOp",EDGE,"E27.right")])],"isStart":false});
            var sketch = newSketch(context, id + "F18", { "sketchPlane" : qUnion([Q0])});
            skLineSegment(sketch, "E50.bottom", {"start": v(1003.3, -533.4) * mm, "end": v(977.9, -533.4) * mm});
            skLineSegment(sketch, "E50.top", {"start": v(1003.3, -508) * mm, "end": v(977.9, -508) * mm});
            skLineSegment(sketch, "E50.left", {"start": v(1003.3, -533.4) * mm, "end": v(1003.3, -508) * mm});
            skLineSegment(sketch, "E50.right", {"start": v(977.9, -533.4) * mm, "end": v(977.9, -508) * mm});
            skLineSegment(sketch, "E51.bottom", {"start": v(1003.3, 533.4) * mm, "end": v(977.9, 533.4) * mm});
            skLineSegment(sketch, "E51.top", {"start": v(1003.3, 508) * mm, "end": v(977.9, 508) * mm});
            skLineSegment(sketch, "E51.left", {"start": v(1003.3, 533.4) * mm, "end": v(1003.3, 508) * mm});
            skLineSegment(sketch, "E51.right", {"start": v(977.9, 533.4) * mm, "end": v(977.9, 508) * mm});
            skLineSegment(sketch, "E52.bottom", {"start": v(-1003.3, -533.4) * mm, "end": v(-977.9, -533.4) * mm});
            skLineSegment(sketch, "E52.top", {"start": v(-1003.3, -508) * mm, "end": v(-977.9, -508) * mm});
            skLineSegment(sketch, "E52.left", {"start": v(-1003.3, -533.4) * mm, "end": v(-1003.3, -508) * mm});
            skLineSegment(sketch, "E52.right", {"start": v(-977.9, -533.4) * mm, "end": v(-977.9, -508) * mm});
            skSolve(sketch);
        }
        {
            var Q0;
            Q0 = qSketchRegion(id + "F18", true);
            extrude(context, id + "F19", {"entities" : qUnion([Q0]), "operationType" : NewBodyOperationType.ADD, "depth" : 254 * mm});
        }
        {
            var Q0;
            Q0=makeQuery(id+"F19.opExtrude","CAP_FACE",FACE,{"disambiguationData":[OSD([sQuery(id+"F18.wireOp",EDGE,"E51.bottom"),sQuery(id+"F18.wireOp",EDGE,"E51.top"),sQuery(id+"F18.wireOp",EDGE,"E51.left"),sQuery(id+"F18.wireOp",EDGE,"E51.right")])],"isStart":false});
            var sketch = newSketch(context, id + "F20", { "sketchPlane" : qUnion([Q0])});
            skLineSegment(sketch, "E53.bottom", {"start": v(977.9, 508) * mm, "end": v(1003.3, 508) * mm});
            skLineSegment(sketch, "E53.top", {"start": v(977.9, -508) * mm, "end": v(1003.3, -508) * mm});
            skLineSegment(sketch, "E53.left", {"start": v(977.9, 508) * mm, "end": v(977.9, -508) * mm});
            skLineSegment(sketch, "E53.right", {"start": v(1003.3, 508) * mm, "end": v(1003.3, -508) * mm});
            skSolve(sketch);
        }
        {
            var Q0;
            Q0 = qSketchRegion(id + "F20", true);
            extrude(context, id + "F21", {"entities" : qUnion([Q0]), "operationType" : NewBodyOperationType.ADD, "oppositeDirection" : true, "depth" : 25.4 * mm});
        }
        {
            var Q0;
            Q0=makeQuery(id+"F21.boolean.opBoolean","MERGE",FACE,{"derivedFrom":[makeQuery(id+"F19.opExtrude","CAP_FACE",FACE,{"disambiguationData":[OSD([sQuery(id+"F18.wireOp",EDGE,"E50.bottom"),sQuery(id+"F18.wireOp",EDGE,"E50.top"),sQuery(id+"F18.wireOp",EDGE,"E50.left"),sQuery(id+"F18.wireOp",EDGE,"E50.right")])],"isStart":false}),makeQuery(id+"F19.opExtrude","CAP_FACE",FACE,{"disambiguationData":[OSD([sQuery(id+"F18.wireOp",EDGE,"E51.bottom"),sQuery(id+"F18.wireOp",EDGE,"E51.top"),sQuery(id+"F18.wireOp",EDGE,"E51.left"),sQuery(id+"F18.wireOp",EDGE,"E51.right")])],"isStart":false}),makeQuery(id+"F21.opExtrude","CAP_FACE",FACE,{"disambiguationData":[OSD([sQuery(id+"F20.wireOp",EDGE,"E53.bottom"),sQuery(id+"F20.wireOp",EDGE,"E53.top"),sQuery(id+"F20.wireOp",EDGE,"E53.left"),sQuery(id+"F20.wireOp",EDGE,"E53.right")])],"isStart":true})]});
            var sketch = newSketch(context, id + "F22", { "sketchPlane" : qUnion([Q0])});
            skPoint(sketch, "E54.0", {"position": v(-977.9, -508) * mm});
            skPoint(sketch, "E55.0", {"position": v(977.9, -533.4) * mm});
            skLineSegment(sketch, "E56.bottom", {"start": v(977.9, -533.4) * mm, "end": v(-977.9, -533.4) * mm});
            skLineSegment(sketch, "E56.top", {"start": v(977.9, -508) * mm, "end": v(-977.9, -508) * mm});
            skLineSegment(sketch, "E56.left", {"start": v(977.9, -533.4) * mm, "end": v(977.9, -508) * mm});
            skLineSegment(sketch, "E56.right", {"start": v(-977.9, -533.4) * mm, "end": v(-977.9, -508) * mm});
            skSolve(sketch);
        }
        {
            var Q0;
            Q0=makeQuery(id+"F22.imprint","IMPRINT",FACE,{"disambiguationData":[TD([[makeQuery(id+"F22.imprint","IMPRINT",EDGE,{"derivedFrom":sQuery(id+"F22.wireOp",EDGE,"E56.bottom")}),-1.0]])]});
            extrude(context, id + "F23", {"entities" : qUnion([Q0]), "operationType" : NewBodyOperationType.ADD, "oppositeDirection" : true, "depth" : 25.4 * mm});
        }
        {
            var Q0;
            Q0=makeQuery(id+"F12.opExtrude","CAP_FACE",FACE,{"disambiguationData":[OSD([sQuery(id+"F11.wireOp",EDGE,"E30.bottom"),sQuery(id+"F11.wireOp",EDGE,"E30.top"),sQuery(id+"F11.wireOp",EDGE,"E30.left"),sQuery(id+"F11.wireOp",EDGE,"E30.right")])],"isStart":false});
            var sketch = newSketch(context, id + "F24", { "sketchPlane" : qUnion([Q0])});
            skLineSegment(sketch, "E57.bottom", {"start": v(540.1, -354.77) * mm, "end": v(852, -354.77) * mm});
            skLineSegment(sketch, "E57.top", {"start": v(540.1, 369.22) * mm, "end": v(852, 369.22) * mm});
            skLineSegment(sketch, "E57.left", {"start": v(540.1, -354.77) * mm, "end": v(540.1, 369.22) * mm});
            skLineSegment(sketch, "E57.right", {"start": v(852, -354.77) * mm, "end": v(852, 369.22) * mm});
            skSolve(sketch);
        }
        {
            var Q0;
            Q0=makeQuery(id+"F24.imprint","IMPRINT",FACE,{"disambiguationData":[TD([[makeQuery(id+"F24.imprint","IMPRINT",EDGE,{"derivedFrom":sQuery(id+"F24.wireOp",EDGE,"E57.bottom")}),1.0]])]});
            extrude(context, id + "F25", {"entities" : qUnion([Q0]), "depth" : 127 * mm});
        }
        {
            var Q0;
            Q0=makeQuery(id+"F25.opExtrude","CAP_EDGE",EDGE,{"disambiguationData":[OSD([sQuery(id+"F24.wireOp",EDGE,"E57.top")])],"isStart":false});
            var Q1;
            Q1=makeQuery(id+"F25.opExtrude","CAP_EDGE",EDGE,{"disambiguationData":[OSD([sQuery(id+"F24.wireOp",EDGE,"E57.bottom")])],"isStart":false});
            var Q2;
            Q2=makeQuery(id+"F25.opExtrude","CAP_EDGE",EDGE,{"disambiguationData":[OSD([sQuery(id+"F24.wireOp",EDGE,"E57.top")])],"isStart":true});
            var Q3;
            Q3=makeQuery(id+"F25.opExtrude","CAP_EDGE",EDGE,{"disambiguationData":[OSD([sQuery(id+"F24.wireOp",EDGE,"E57.bottom")])],"isStart":true});
            var Q4;
            Q4=makeQuery(id+"F25.opExtrude","CAP_EDGE",EDGE,{"disambiguationData":[OSD([sQuery(id+"F24.wireOp",EDGE,"E57.right")])],"isStart":false});
            var Q5;
            Q5=makeQuery(id+"F25.opExtrude","CAP_EDGE",EDGE,{"disambiguationData":[OSD([sQuery(id+"F24.wireOp",EDGE,"E57.right")])],"isStart":true});
            var Q6;
            Q6=makeQuery(id+"F25.opExtrude","CAP_EDGE",EDGE,{"disambiguationData":[OSD([sQuery(id+"F24.wireOp",EDGE,"E57.left")])],"isStart":true});
            var Q7;
            Q7=makeQuery(id+"F25.opExtrude","CAP_EDGE",EDGE,{"disambiguationData":[OSD([sQuery(id+"F24.wireOp",EDGE,"E57.left")])],"isStart":false});
            fillet(context, id + "F26", {"entities" : qUnion([Q0, Q1, Q2, Q3, Q4, Q5, Q6, Q7]), "radius" : 63.5 * mm, "tangentPropagation" : true, "rho" : .25, "crossSection" : FilletCrossSection.CONIC, "allowEdgeOverflow" : false});
        }
        {
            var Q0;
            Q0=makeQuery(id+"F1.opExtrude","SWEPT_FACE",FACE,{"disambiguationData":[OSD([sQuery(id+"F0.wireOp",EDGE,"E3.bottom")])]});
            var sketch = newSketch(context, id + "F27", { "sketchPlane" : qUnion([Q0])});
            skLineSegment(sketch, "E58", {"start": v(1003.3, 0) * mm, "end": v(1003.3, 558.8) * mm});
            skLineSegment(sketch, "E59", {"start": v(1003.3, 558.8) * mm, "end": v(546.1, 558.8) * mm});
            skLineSegment(sketch, "E60", {"start": v(546.1, 558.8) * mm, "end": v(546.1, 577.85) * mm});
            skLineSegment(sketch, "E61", {"start": v(546.1, 577.85) * mm, "end": v(1003.3, 577.85) * mm});
            skLineSegment(sketch, "E62", {"start": v(1003.3, 577.85) * mm, "end": v(1003.3, 558.8) * mm});
            skSolve(sketch);
        }
        {
            var Q0;
            {var subQ0=sQuery(id+"F27.wireOp",EDGE,"E60");Q0=makeQuery(id+"F27.imprint","IMPRINT",FACE,{"disambiguationData":[TD([[makeQuery(id+"F27.imprint","IMPRINT",EDGE,{"derivedFrom":subQ0}),-1.0]])]});}
            var Q1;
            {var subQ0=sQuery(id+"F27.wireOp",EDGE,"E62");Q1=makeQuery(id+"F27.imprint","IMPRINT",FACE,{"disambiguationData":[TD([[makeQuery(id+"F27.imprint","IMPRINT",EDGE,{"derivedFrom":subQ0}),-1.0]])]});}
            extrude(context, id + "F28", {"entities" : qUnion([Q0, Q1]), "depth" : 965.2 * mm});
        }
        {
            var Q0;
            Q0=makeQuery(id+"F28.opExtrude","CAP_EDGE",EDGE,{"disambiguationData":[OSD([sQuery(id+"F27.wireOp",EDGE,"E60")])],"isStart":false});
            fillet(context, id + "F29", {"entities" : qUnion([Q0]), "radius" : 101.6 * mm, "tangentPropagation" : true, "allowEdgeOverflow" : false});
        }
        {
            var Q0;
            Q0=makeQuery(id+"F28.opExtrude","CAP_FACE",FACE,{"disambiguationData":[OSD([sQuery(id+"F27.wireOp",EDGE,"E59"),sQuery(id+"F27.wireOp",EDGE,"E60"),sQuery(id+"F27.wireOp",EDGE,"E61"),sQuery(id+"F27.wireOp",EDGE,"E62")])],"isStart":true});
            var sketch = newSketch(context, id + "F30", { "sketchPlane" : qUnion([Q0])});
            skLineSegment(sketch, "E63.bottom", {"start": v(-546.1, 558.8) * mm, "end": v(-952.5, 558.8) * mm});
            skLineSegment(sketch, "E63.top", {"start": v(-546.1, 1270) * mm, "end": v(-952.5, 1270) * mm});
            skLineSegment(sketch, "E63.left", {"start": v(-546.1, 558.8) * mm, "end": v(-546.1, 1270) * mm});
            skLineSegment(sketch, "E63.right", {"start": v(-952.5, 558.8) * mm, "end": v(-952.5, 1270) * mm});
            skSolve(sketch);
        }
        {
            var Q0;
            Q0 = qSketchRegion(id + "F30", true);
            extrude(context, id + "F31", {"entities" : qUnion([Q0]), "depth" : 50.8 * mm});
        }
        {
            var Q0;
            Q0=makeQuery(id+"F31.opExtrude","CAP_FACE",FACE,{"disambiguationData":[OSD([sQuery(id+"F30.wireOp",EDGE,"E63.bottom"),sQuery(id+"F30.wireOp",EDGE,"E63.top"),sQuery(id+"F30.wireOp",EDGE,"E63.left"),sQuery(id+"F30.wireOp",EDGE,"E63.right")])],"isStart":true});
            var sketch = newSketch(context, id + "F32", { "sketchPlane" : qUnion([Q0])});
            skLineSegment(sketch, "E64.bottom", {"start": v(546.1, 1270) * mm, "end": v(565.15, 1270) * mm});
            skLineSegment(sketch, "E64.top", {"start": v(546.1, 577.85) * mm, "end": v(565.15, 577.85) * mm});
            skLineSegment(sketch, "E64.left", {"start": v(546.1, 1270) * mm, "end": v(546.1, 577.85) * mm});
            skLineSegment(sketch, "E64.right", {"start": v(565.15, 1270) * mm, "end": v(565.15, 577.85) * mm});
            skLineSegment(sketch, "E65.bottom", {"start": v(952.5, 1270) * mm, "end": v(933.45, 1270) * mm});
            skLineSegment(sketch, "E65.top", {"start": v(952.5, 577.85) * mm, "end": v(933.45, 577.85) * mm});
            skLineSegment(sketch, "E65.left", {"start": v(952.5, 1270) * mm, "end": v(952.5, 577.85) * mm});
            skLineSegment(sketch, "E65.right", {"start": v(933.45, 1270) * mm, "end": v(933.45, 577.85) * mm});
            skLineSegment(sketch, "E66.bottom", {"start": v(565.15, 577.85) * mm, "end": v(742.95, 577.85) * mm});
            skLineSegment(sketch, "E66.top", {"start": v(565.15, 755.65) * mm, "end": v(742.95, 755.65) * mm});
            skLineSegment(sketch, "E66.left", {"start": v(565.15, 577.85) * mm, "end": v(565.15, 755.65) * mm});
            skLineSegment(sketch, "E66.right", {"start": v(742.95, 577.85) * mm, "end": v(742.95, 755.65) * mm});
            skLineSegment(sketch, "E67.bottom", {"start": v(933.45, 577.85) * mm, "end": v(755.65, 577.85) * mm});
            skLineSegment(sketch, "E67.top", {"start": v(933.45, 755.65) * mm, "end": v(755.65, 755.65) * mm});
            skLineSegment(sketch, "E67.left", {"start": v(933.45, 577.85) * mm, "end": v(933.45, 755.65) * mm});
            skLineSegment(sketch, "E67.right", {"start": v(755.65, 577.85) * mm, "end": v(755.65, 755.65) * mm});
            skLineSegment(sketch, "E68.0.1.0", {"start": v(565.15, 946.15) * mm, "end": v(742.95, 946.15) * mm});
            skLineSegment(sketch, "E68.0.1.1", {"start": v(565.15, 768.35) * mm, "end": v(742.95, 768.35) * mm});
            skLineSegment(sketch, "E68.0.1.2", {"start": v(742.95, 768.35) * mm, "end": v(742.95, 946.15) * mm});
            skLineSegment(sketch, "E68.0.1.3", {"start": v(755.65, 768.35) * mm, "end": v(755.65, 946.15) * mm});
            skLineSegment(sketch, "E68.0.1.4", {"start": v(933.45, 946.15) * mm, "end": v(755.65, 946.15) * mm});
            skLineSegment(sketch, "E68.0.1.5", {"start": v(933.45, 1460.5) * mm, "end": v(933.45, 768.35) * mm});
            skLineSegment(sketch, "E68.0.1.6", {"start": v(933.45, 768.35) * mm, "end": v(755.65, 768.35) * mm});
            skLineSegment(sketch, "E68.0.2.0", {"start": v(565.15, 1136.65) * mm, "end": v(742.95, 1136.65) * mm});
            skLineSegment(sketch, "E68.0.2.1", {"start": v(565.15, 958.85) * mm, "end": v(742.95, 958.85) * mm});
            skLineSegment(sketch, "E68.0.2.2", {"start": v(742.95, 958.85) * mm, "end": v(742.95, 1136.65) * mm});
            skLineSegment(sketch, "E68.0.2.3", {"start": v(755.65, 958.85) * mm, "end": v(755.65, 1136.65) * mm});
            skLineSegment(sketch, "E68.0.2.4", {"start": v(933.45, 1136.65) * mm, "end": v(755.65, 1136.65) * mm});
            skLineSegment(sketch, "E68.0.2.5", {"start": v(933.45, 1651) * mm, "end": v(933.45, 958.85) * mm});
            skLineSegment(sketch, "E68.0.2.6", {"start": v(933.45, 958.85) * mm, "end": v(755.65, 958.85) * mm});
            skLineSegment(sketch, "E68.direction1", {"start": v(565.15, 755.65) * mm, "end": v(590.55, 755.65) * mm, "construction": true});
            skLineSegment(sketch, "E68.direction2", {"start": v(565.15, 755.65) * mm, "end": v(565.15, 946.15) * mm, "construction": true});
            skLineSegment(sketch, "E69", {"start": v(565.15, 1136.65) * mm, "end": v(565.15, 1149.35) * mm});
            skLineSegment(sketch, "E70", {"start": v(565.15, 1149.35) * mm, "end": v(933.45, 1149.35) * mm});
            skSolve(sketch);
        }
        {
            var Q0;
            {var subQ3=sQuery(id+"F32.wireOp",EDGE,"E70");Q0=makeQuery(id+"F32.imprint","IMPRINT",FACE,{"disambiguationData":[TD([[makeQuery(id+"F32.imprint","IMPRINT",EDGE,{"derivedFrom":subQ3}),1.0]])]});}
            var Q1;
            {var subQ0=sQuery(id+"F32.wireOp",EDGE,"E68.0.2.0");Q1=makeQuery(id+"F32.imprint","IMPRINT",FACE,{"disambiguationData":[TD([[makeQuery(id+"F32.imprint","IMPRINT",EDGE,{"derivedFrom":subQ0}),-1.0]])]});}
            var Q2;
            Q2=makeQuery(id+"F32.imprint","IMPRINT",FACE,{"disambiguationData":[TD([[makeQuery(id+"F32.imprint","IMPRINT",EDGE,{"derivedFrom":sQuery(id+"F32.wireOp",EDGE,"E68.0.2.3")}),-1.0]])]});
            var Q3;
            Q3=makeQuery(id+"F32.imprint","IMPRINT",FACE,{"disambiguationData":[TD([[makeQuery(id+"F32.imprint","IMPRINT",EDGE,{"derivedFrom":sQuery(id+"F32.wireOp",EDGE,"E68.0.1.3")}),-1.0]])]});
            var Q4;
            {var subQ0=sQuery(id+"F32.wireOp",EDGE,"E68.0.1.0");Q4=makeQuery(id+"F32.imprint","IMPRINT",FACE,{"disambiguationData":[TD([[makeQuery(id+"F32.imprint","IMPRINT",EDGE,{"derivedFrom":subQ0}),-1.0]])]});}
            var Q5;
            Q5=makeQuery(id+"F32.imprint","IMPRINT",FACE,{"disambiguationData":[TD([[makeQuery(id+"F32.imprint","IMPRINT",EDGE,{"derivedFrom":sQuery(id+"F32.wireOp",EDGE,"E66.bottom")}),1.0]])]});
            var Q6;
            Q6=makeQuery(id+"F32.imprint","IMPRINT",FACE,{"disambiguationData":[TD([[makeQuery(id+"F32.imprint","IMPRINT",EDGE,{"derivedFrom":sQuery(id+"F32.wireOp",EDGE,"E67.bottom")}),-1.0]])]});
            extrude(context, id + "F33", {"entities" : qUnion([Q0, Q1, Q2, Q3, Q4, Q5, Q6]), "operationType" : NewBodyOperationType.REMOVE, "oppositeDirection" : true, "depth" : 44.45 * mm});
        }
    });
